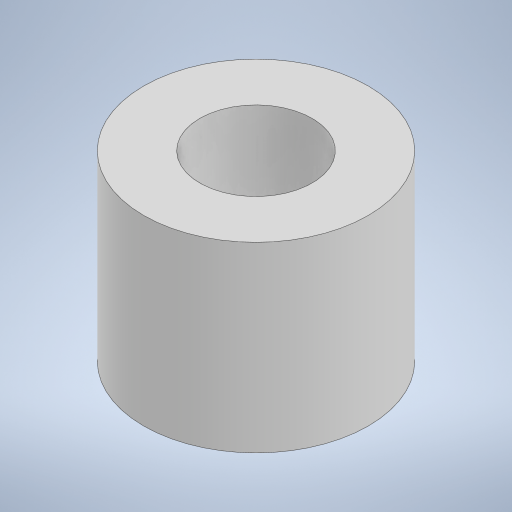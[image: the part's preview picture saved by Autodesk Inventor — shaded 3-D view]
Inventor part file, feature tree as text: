
AUTODESK INVENTOR PART (.ipt)
format: ipt  version: 2024 (Build 280153000, 153)  size: 533,504 bytes
history: native  units: mm
features: extrude x1, sketch x1
ambient origin geometry x8: Origin, YZ Plane, XZ Plane, XY Plane, X Axis, Y Axis, Z Axis, Center Point
bodies: Solid1 (feature_tree)
feature tree (2):
  extrude  "Extrusion1"  Depth=8.0mm
  sketch  "Sketch1"  dims[d0=16.0mm d1=8.0mm d2=13.0mm d3=0.0mm]
